# Revit family: Pressure_Reducing_Valve-Zurn_Wilkins-Model_NR3XLDU_Threaded-(12-2_Inch)
name_source: partatom
category: Pipe Accessories
units: mm (PartAtom-declared; Revit-internal decimal feet)

## family parameters
Always vertical = Yes
Cut with Voids When Loaded = No
OmniClass Number = 23.65.55.14.17
OmniClass Title = Adjusting/Controlling Valves for Liquid Services
Part Type = Valve - Breaks Into
Round Connector Dimension = Use Radius
Shared = No
Work Plane-Based = No

## types (6) — shared parameters
Assembly Code = D2020300
Default Elevation = 0' - 0"
Description = Water Pressure Reducing Valve with Integral By-Pass Check Valve and Strainer
Factory Preset Pressure = 50.00 psi
Flow Rate (GPM) = 0 GPM
Main Material = Paint - Zurn - Bronze
Manufacturer = Zurn Water, LLC
Manufacturer Brand = Zurn Wilkins
Max Working Water Temperature = 140 °F
Model = NR3XLDU
Modified Date = 08/11/2025
Product Documentation Link = https://files.zurn.com
Product Installation Sheet URL = https://files.zurn.com
Product Page URL = https://www.zurn.com
Product data URL = https://www.bimobject.com
Repair Parts URL = https://files.zurn.com

## per-type parameters (varying)
- 2-NR3XLDU (2" NR3XLDU): Bell Base Length=0' - 0 1/4"; Bell Base Radius=0' - 1 21/32"; Bell Blend Radius=0' - 1 1/4"; Bell Hex Radius=0' - 1 1/4"; Bell Upper Base Length=0' - 2 1/32"; Bell Upper Base Radius=0' - 1 1/4"; Body Base Tail Radius=0' - 1 3/16"; Body Radius=0' - 1 7/16"; Body Seat Bell Length=0' - 1"; Body Tail Radius=0' - 0 7/16"; Body Top Length=0' - 1 23/32"; Body Top Radius=0' - 1 7/16"; Body Top Seat Bell Radius=0' - 1 7/8"; Body Width=0' - 0 17/32"; Center to Nut End Length=0' - 3 1/16"; DIM A - Overall length of the valve=0' - 7 1/2"; DIM B -Total height of the valve=0' - 8 1/2"; DIM C - Body Center to bottom=0' - 2"; DIM D - Bell base diameter=0' - 3 3/4"; Length=0' - 5"; MR Hex nut width=0' - 2"; MR hex nut thickness=0' - 0 7/8"; Max Working Water Pressure=300.00 psi; Nominal Diameter=0' - 2"; Nominal Radius=0' - 1"; Nut Size=Nut : 2 inch; Polygon diameter=0' - 2 1/4"; Product Weight (lbs)=10; Reduced Pressure Range=25 to 75 psi; Tailpiece Center to End Left side=0' - 3 3/4"; Tailpiece Center to End Right side Length=0' - 3 3/4"; Tailpiece radius=0' - 1 3/8"; URL=http://www.zurn.com
- 112-NR3XLDU (1-1/2" NR3XLDU): Bell Base Length=0' - 0 1/4"; Bell Base Radius=0' - 1 21/32"; Bell Blend Radius=0' - 1 1/4"; Bell Hex Radius=0' - 1 1/4"; Bell Upper Base Length=0' - 2 1/32"; Bell Upper Base Radius=0' - 1 1/4"; Body Base Tail Radius=0' - 1 3/16"; Body Radius=0' - 1 3/16"; Body Seat Bell Length=0' - 1"; Body Tail Radius=0' - 0 7/16"; Body Top Length=0' - 1 25/32"; Body Top Radius=0' - 1 7/16"; Body Top Seat Bell Radius=0' - 1 7/8"; Body Width=0' - 0 13/32"; Center to Nut End Length=0' - 3 1/16"; DIM A - Overall length of the valve=0' - 7 1/2"; DIM B -Total height of the valve=0' - 8 1/2"; DIM C - Body Center to bottom=0' - 1 3/4"; DIM D - Bell base diameter=0' - 3 3/4"; Length=0' - 5"; MR Hex nut width=0' - 1 11/16"; MR hex nut thickness=0' - 0 7/8"; Max Working Water Pressure=300.00 psi; Nominal Diameter=0' - 1 1/2"; Nominal Radius=0' - 0 3/4"; Nut Size=Nut : 1 1/2 inch; Polygon diameter=0' - 3 3/8"; Product Weight (lbs)=8; Reduced Pressure Range=25 to 75 psi; Tailpiece Center to End Left side=0' - 3 3/4"; Tailpiece Center to End Right side Length=0' - 3 3/4"; Tailpiece radius=0' - 1 3/8"; URL=http://www.zurn.com
- 114-NR3XLDU (1-1/4" NR3XLDU): Bell Base Length=0' - 0 3/16"; Bell Base Radius=0' - 1 3/8"; Bell Blend Radius=0' - 0 7/8"; Bell Hex Radius=0' - 0 31/32"; Bell Upper Base Length=0' - 2 1/32"; Bell Upper Base Radius=0' - 1"; Body Base Tail Radius=0' - 0 13/16"; Body Radius=0' - 1"; Body Seat Bell Length=0' - 0 7/8"; Body Tail Radius=0' - 0 7/16"; Body Top Length=0' - 1 3/8"; Body Top Radius=0' - 1 7/32"; Body Top Seat Bell Radius=0' - 1 1/2"; Body Width=0' - 0 7/16"; Center to Nut End Length=0' - 2 7/8"; DIM A - Overall length of the valve=0' - 7 3/8"; DIM B -Total height of the valve=0' - 7 3/4"; DIM C - Body Center to bottom=0' - 1 3/16"; DIM D - Bell base diameter=0' - 3"; Length=0' - 5"; MR Hex nut width=0' - 1 3/8"; MR hex nut thickness=0' - 0 11/16"; Max Working Water Pressure=400.00 psi; Nominal Diameter=0' - 1 1/4"; Nominal Radius=0' - 0 5/8"; Nut Size=Nut : 1 1/4 inch; Polygon diameter=0' - 2 1/4"; Product Weight (lbs)=6; Reduced Pressure Range=15 to 75 psi; Tailpiece Center to End Left side=0' - 3 5/8"; Tailpiece Center to End Right side Length=0' - 3 5/8"; Tailpiece radius=0' - 0 25/32"; URL=http://www.zurn.com
- 1-NR3XLDU (1" NR3XLDU): Bell Base Length=0' - 0 3/16"; Bell Base Radius=0' - 1 1/32"; Bell Blend Radius=0' - 0 3/4"; Bell Hex Radius=0' - 0 13/16"; Bell Upper Base Length=0' - 1 3/16"; Bell Upper Base Radius=0' - 0 7/8"; Body Base Tail Radius=0' - 0 13/16"; Body Radius=0' - 0 27/32"; Body Seat Bell Length=0' - 0 15/32"; Body Tail Radius=0' - 0 7/16"; Body Top Length=0' - 1 5/32"; Body Top Radius=0' - 1"; Body Top Seat Bell Radius=0' - 1 1/4"; Body Width=0' - 0 17/32"; Center to Nut End Length=0' - 2 1/4"; DIM A - Overall length of the valve=0' - 5 15/16"; DIM B -Total height of the valve=0' - 6 1/4"; DIM C - Body Center to bottom=0' - 1 1/8"; DIM D - Bell base diameter=0' - 2 1/2"; Length=0' - 4"; MR Hex nut width=0' - 1"; MR hex nut thickness=0' - 0 21/32"; Max Working Water Pressure=400.00 psi; Nominal Diameter=0' - 1"; Nominal Radius=0' - 0 1/2"; Nut Size=Nut : 1 inch; Polygon diameter=0' - 2 1/4"; Product Weight (lbs)=5; Reduced Pressure Range=15 to 75 psi; Tailpiece Center to End Left side=0' - 2 31/32"; Tailpiece Center to End Right side Length=0' - 2 31/32"; Tailpiece radius=0' - 0 21/32"; URL=http://www.zurn.com
- 34-NR3XLDU (3/4" NR3XLDU): Bell Base Length=0' - 0 3/16"; Bell Base Radius=0' - 1 1/32"; Bell Blend Radius=0' - 0 3/4"; Bell Hex Radius=0' - 0 13/16"; Bell Upper Base Length=0' - 1 3/16"; Bell Upper Base Radius=0' - 0 7/8"; Body Base Tail Radius=0' - 0 5/8"; Body Radius=0' - 0 11/16"; Body Seat Bell Length=0' - 0 1/2"; Body Tail Radius=0' - 0 11/32"; Body Top Length=0' - 1 5/32"; Body Top Radius=0' - 1 1/16"; Body Top Seat Bell Radius=0' - 1 1/4"; Body Width=0' - 0 3/8"; Center to Nut End Length=0' - 2 1/8"; DIM A - Overall length of the valve=0' - 5 3/8"; DIM B -Total height of the valve=0' - 6 1/4"; DIM C - Body Center to bottom=0' - 1 1/8"; DIM D - Bell base diameter=0' - 2 1/2"; Length=0' - 3 1/2"; MR Hex nut width=0' - 0 7/8"; MR hex nut thickness=0' - 0 5/8"; Max Working Water Pressure=400.00 psi; Nominal Diameter=0' - 0 3/4"; Nominal Radius=0' - 0 3/8"; Nut Size=Nut : 3/4 inch; Polygon diameter=0' - 2 1/4"; Product Weight (lbs)=3; Reduced Pressure Range=15 to 75 psi; Tailpiece Center to End Left side=0' - 2 11/16"; Tailpiece Center to End Right side Length=0' - 2 11/16"; Tailpiece radius=0' - 0 5/8"; URL=http://www.zurn.com
- 12-NR3XLDU (1/2" NR3XLDU): Bell Base Length=0' - 0 3/16"; Bell Base Radius=0' - 1 1/32"; Bell Blend Radius=0' - 0 3/4"; Bell Hex Radius=0' - 0 13/16"; Bell Upper Base Length=0' - 1 3/16"; Bell Upper Base Radius=0' - 0 7/8"; Body Base Tail Radius=0' - 0 5/8"; Body Radius=0' - 0 11/16"; Body Seat Bell Length=0' - 0 15/32"; Body Tail Radius=0' - 0 7/16"; Body Top Length=0' - 1 5/32"; Body Top Radius=0' - 1 1/16"; Body Top Seat Bell Radius=0' - 1 1/4"; Body Width=0' - 0 7/16"; Center to Nut End Length=0' - 2 1/16"; DIM A - Overall length of the valve=0' - 5 1/4"; DIM B -Total height of the valve=0' - 6 1/4"; DIM C - Body Center to bottom=0' - 1 1/8"; DIM D - Bell base diameter=0' - 2 1/2"; Length=0' - 3 1/2"; MR Hex nut width=0' - 0 7/8"; MR hex nut thickness=0' - 0 5/8"; Max Working Water Pressure=400.00 psi; Nominal Diameter=0' - 0 1/2"; Nominal Radius=0' - 0 1/4"; Nut Size=Nut : 1/2 inch; Polygon diameter=0' - 1 3/4"; Product Weight (lbs)=3; Reduced Pressure Range=15 to 75 psi; Tailpiece Center to End Left side=0' - 2 5/8"; Tailpiece Center to End Right side Length=0' - 2 5/8"; Tailpiece radius=0' - 0 17/32"; URL=https://www.zurn.com

## geometry (parser evidence)
native form markers: Blend x1, Sweep x7
no freeform markers — native parametric forms only
